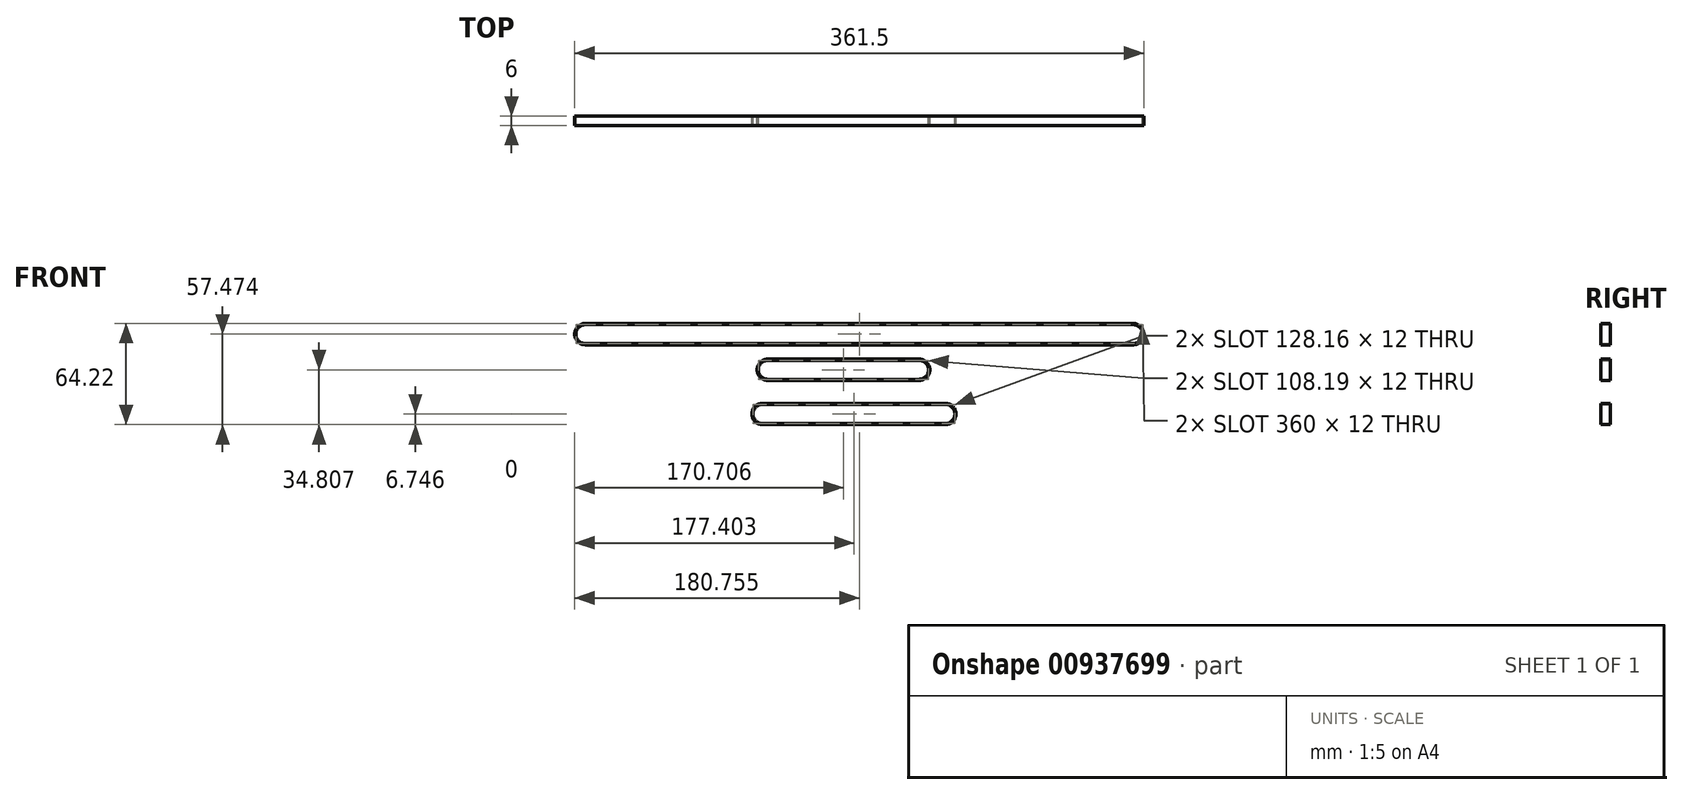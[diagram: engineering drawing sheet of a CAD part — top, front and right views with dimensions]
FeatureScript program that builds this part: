
annotation { "Feature Type Name" : "Feature", "Feature Type Description" : "" }
export const myFeature = defineFeature(function(context is Context, id is Id, definition is map)
    precondition{}
    {
        {
            var Q0;
            Q0=qCreatedBy(makeId("Front.planeOp"),FACE);
            var sketch = newSketch(context, id + "F0", { "sketchPlane" : qUnion([Q0])});
            skLineSegment(sketch, "E0", {"start": v(-166.09, 3.58) * mm, "end": v(181.91, 3.58) * mm});
            skArc(sketch, "E1", {"start": v(-166.09, 9.58) * mm, "mid": v(-172.09, 3.58) * mm, "end": v(-166.09, -2.42) * mm});
            skArc(sketch, "E2", {"start": v(181.91, -2.42) * mm, "mid": v(187.91, 3.58) * mm, "end": v(181.91, 9.58) * mm});
            skLineSegment(sketch, "E3", {"start": v(-166.09, 9.58) * mm, "end": v(181.91, 9.58) * mm});
            skLineSegment(sketch, "E4", {"start": v(181.91, -2.42) * mm, "end": v(-166.09, -2.42) * mm});
            skArc(sketch, "E5.0", {"start": v(-166.09, 10.33) * mm, "mid": v(-172.84, 3.58) * mm, "end": v(-166.09, -3.17) * mm});
            skLineSegment(sketch, "E5.1", {"start": v(-166.09, 10.33) * mm, "end": v(181.91, 10.33) * mm});
            skArc(sketch, "E5.2", {"start": v(181.91, -3.17) * mm, "mid": v(188.66, 3.58) * mm, "end": v(181.91, 10.33) * mm});
            skLineSegment(sketch, "E5.3", {"start": v(181.91, -3.17) * mm, "end": v(-166.09, -3.17) * mm});
            skSolve(sketch);
        }
        {
            var Q0;
            Q0=makeQuery(id+"F0.imprint","IMPRINT",FACE,{"disambiguationData":[TD([[makeQuery(id+"F0.imprint","IMPRINT",EDGE,{"derivedFrom":sQuery(id+"F0.wireOp",EDGE,"E1")}),-1.0]])]});
            extrude(context, id + "F1", {"entities" : qUnion([Q0]), "depth" : 6 * mm, "offsetDistance" : 25 * mm});
        }
        {
            var Q0;
            Q0=qCreatedBy(makeId("Front.planeOp"),FACE);
            var sketch = newSketch(context, id + "F2", { "sketchPlane" : qUnion([Q0])});
            skArc(sketch, "E6", {"start": v(-50.23, -13.08) * mm, "mid": v(-56.23, -19.08) * mm, "end": v(-50.23, -25.08) * mm});
            skArc(sketch, "E7", {"start": v(45.96, -25.08) * mm, "mid": v(51.96, -19.08) * mm, "end": v(45.96, -13.08) * mm});
            skLineSegment(sketch, "E8", {"start": v(-50.23, -13.08) * mm, "end": v(45.96, -13.08) * mm});
            skLineSegment(sketch, "E9", {"start": v(-50.23, -25.08) * mm, "end": v(45.96, -25.08) * mm});
            skLineSegment(sketch, "E10.0", {"start": v(-50.23, -12.33) * mm, "end": v(45.96, -12.33) * mm});
            skArc(sketch, "E10.1", {"start": v(-50.23, -12.33) * mm, "mid": v(-56.98, -19.08) * mm, "end": v(-50.23, -25.83) * mm});
            skLineSegment(sketch, "E10.2", {"start": v(-50.23, -25.83) * mm, "end": v(45.96, -25.83) * mm});
            skArc(sketch, "E10.3", {"start": v(45.96, -25.83) * mm, "mid": v(52.71, -19.08) * mm, "end": v(45.96, -12.33) * mm});
            skSolve(sketch);
        }
        {
            var Q0;
            Q0=makeQuery(id+"F2.imprint","IMPRINT",FACE,{"disambiguationData":[TD([[makeQuery(id+"F2.imprint","IMPRINT",EDGE,{"derivedFrom":sQuery(id+"F2.wireOp",EDGE,"E6")}),-1.0]])]});
            extrude(context, id + "F3", {"entities" : qUnion([Q0]), "depth" : 6 * mm, "offsetDistance" : 25 * mm});
        }
        {
            var Q0;
            Q0=qCreatedBy(makeId("Front.planeOp"),FACE);
            var sketch = newSketch(context, id + "F4", { "sketchPlane" : qUnion([Q0])});
            skArc(sketch, "E11", {"start": v(-53.52, -40.4) * mm, "mid": v(-60.27, -47.14) * mm, "end": v(-53.52, -53.9) * mm});
            skArc(sketch, "E12", {"start": v(62.65, -53.9) * mm, "mid": v(69.4, -47.14) * mm, "end": v(62.65, -40.4) * mm});
            skLineSegment(sketch, "E13", {"start": v(-53.52, -40.4) * mm, "end": v(62.65, -40.4) * mm});
            skLineSegment(sketch, "E14", {"start": v(-53.52, -53.9) * mm, "end": v(62.65, -53.9) * mm});
            skArc(sketch, "E15.0", {"start": v(-53.52, -41.14) * mm, "mid": v(-59.52, -47.14) * mm, "end": v(-53.52, -53.14) * mm});
            skLineSegment(sketch, "E15.1", {"start": v(-53.52, -41.14) * mm, "end": v(62.65, -41.14) * mm});
            skArc(sketch, "E15.2", {"start": v(62.65, -53.14) * mm, "mid": v(68.65, -47.14) * mm, "end": v(62.65, -41.14) * mm});
            skLineSegment(sketch, "E15.3", {"start": v(-53.52, -53.14) * mm, "end": v(62.65, -53.14) * mm});
            skSolve(sketch);
        }
        {
            var Q0;
            Q0=makeQuery(id+"F4.imprint","IMPRINT",FACE,{"disambiguationData":[TD([[makeQuery(id+"F4.imprint","IMPRINT",EDGE,{"derivedFrom":sQuery(id+"F4.wireOp",EDGE,"E11")}),1.0]])]});
            extrude(context, id + "F5", {"entities" : qUnion([Q0]), "depth" : 6 * mm, "offsetDistance" : 25 * mm});
        }
    });
